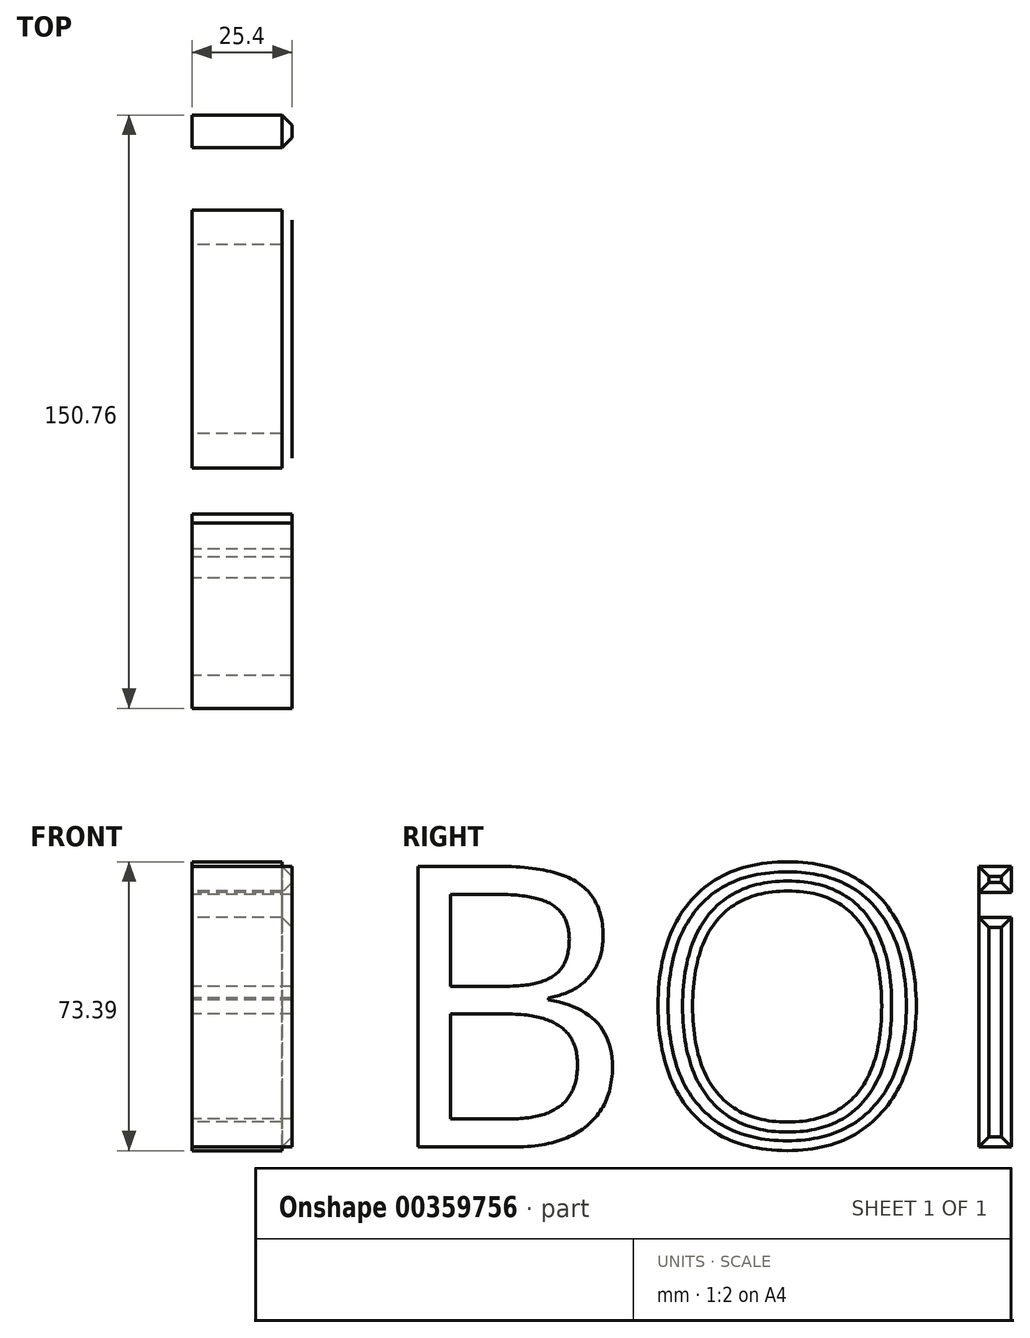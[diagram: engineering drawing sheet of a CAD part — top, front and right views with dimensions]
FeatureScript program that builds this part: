
annotation { "Feature Type Name" : "Feature", "Feature Type Description" : "" }
export const myFeature = defineFeature(function(context is Context, id is Id, definition is map)
    precondition{}
    {
        {
            var Q0;
            Q0=qCreatedBy(makeId("Right.planeOp"),FACE);
            var sketch = newSketch(context, id + "F0", { "sketchPlane" : qUnion([Q0])});
            skText(sketch, "E0", { "text": "BOI\n", "fontName": "OpenSans-Regular.ttf"});
            const initialGuessF0  = {"E0": [-0.0584, -0.03796, 1, 0, 0.0719]};
            skSetInitialGuess(sketch, initialGuessF0);
            skSolve(sketch);
        }
        {
            var Q0;
            Q0 = qSketchRegion(id + "F0", true);
            extrude(context, id + "F1", {"entities" : qUnion([Q0]), "endBound" : BoundingType.SYMMETRIC, "depth" : 25.4 * mm});
        }
        {
            var Q0;
            Q0=makeQuery(id+"F1.opExtrude","CAP_FACE",FACE,{"disambiguationData":[OSD([sQuery(id+"F0.wireOp",EDGE,"E0.sketch_text.stroke-41"),sQuery(id+"F0.wireOp",EDGE,"E0.sketch_text.stroke-42"),sQuery(id+"F0.wireOp",EDGE,"E0.sketch_text.stroke-43"),sQuery(id+"F0.wireOp",EDGE,"E0.sketch_text.stroke-44")])],"isStart":false});
            var sketch = newSketch(context, id + "F2", { "sketchPlane" : qUnion([Q0])});
            skLineSegment(sketch, "E1.bottom", {"start": v(93.88, 26.68) * mm, "end": v(102.17, 26.68) * mm});
            skLineSegment(sketch, "E1.top", {"start": v(93.88, 20.3) * mm, "end": v(102.17, 20.3) * mm});
            skLineSegment(sketch, "E1.left", {"start": v(93.88, 26.68) * mm, "end": v(93.88, 20.3) * mm});
            skLineSegment(sketch, "E1.right", {"start": v(102.17, 26.68) * mm, "end": v(102.17, 20.3) * mm});
            skSolve(sketch);
        }
        {
            var Q0;
            Q0=makeQuery(id+"F2.imprint","IMPRINT",FACE,{"disambiguationData":[TD([[makeQuery(id+"F2.imprint","IMPRINT",EDGE,{"derivedFrom":sQuery(id+"F2.wireOp",EDGE,"E1.bottom")}),-1.0]])]});
            extrude(context, id + "F3", {"entities" : qUnion([Q0]), "operationType" : NewBodyOperationType.REMOVE, "oppositeDirection" : true, "depth" : 25.4 * mm});
        }
        {
            var Q0;
            Q0=makeQuery(id+"F1.opExtrude","CAP_FACE",FACE,{"disambiguationData":[OSD([sQuery(id+"F0.wireOp",EDGE,"E0.sketch_text.stroke-0"),sQuery(id+"F0.wireOp",EDGE,"E0.sketch_text.stroke-1"),sQuery(id+"F0.wireOp",EDGE,"E0.sketch_text.stroke-2"),sQuery(id+"F0.wireOp",EDGE,"E0.sketch_text.stroke-3"),sQuery(id+"F0.wireOp",EDGE,"E0.sketch_text.stroke-4"),sQuery(id+"F0.wireOp",EDGE,"E0.sketch_text.stroke-5"),sQuery(id+"F0.wireOp",EDGE,"E0.sketch_text.stroke-6"),sQuery(id+"F0.wireOp",EDGE,"E0.sketch_text.stroke-7"),sQuery(id+"F0.wireOp",EDGE,"E0.sketch_text.stroke-8"),sQuery(id+"F0.wireOp",EDGE,"E0.sketch_text.stroke-9"),sQuery(id+"F0.wireOp",EDGE,"E0.sketch_text.stroke-10"),sQuery(id+"F0.wireOp",EDGE,"E0.sketch_text.stroke-11"),sQuery(id+"F0.wireOp",EDGE,"E0.sketch_text.stroke-12"),sQuery(id+"F0.wireOp",EDGE,"E0.sketch_text.stroke-13"),sQuery(id+"F0.wireOp",EDGE,"E0.sketch_text.stroke-14"),sQuery(id+"F0.wireOp",EDGE,"E0.sketch_text.stroke-15"),sQuery(id+"F0.wireOp",EDGE,"E0.sketch_text.stroke-16"),sQuery(id+"F0.wireOp",EDGE,"E0.sketch_text.stroke-17"),sQuery(id+"F0.wireOp",EDGE,"E0.sketch_text.stroke-18"),sQuery(id+"F0.wireOp",EDGE,"E0.sketch_text.stroke-19"),sQuery(id+"F0.wireOp",EDGE,"E0.sketch_text.stroke-20"),sQuery(id+"F0.wireOp",EDGE,"E0.sketch_text.stroke-21"),sQuery(id+"F0.wireOp",EDGE,"E0.sketch_text.stroke-22"),sQuery(id+"F0.wireOp",EDGE,"E0.sketch_text.stroke-23"),sQuery(id+"F0.wireOp",EDGE,"E0.sketch_text.stroke-24")])],"isStart":false});
            var Q1;
            Q1=makeQuery(id+"F1.opExtrude","CAP_FACE",FACE,{"disambiguationData":[OSD([sQuery(id+"F0.wireOp",EDGE,"E0.sketch_text.stroke-25"),sQuery(id+"F0.wireOp",EDGE,"E0.sketch_text.stroke-26"),sQuery(id+"F0.wireOp",EDGE,"E0.sketch_text.stroke-27"),sQuery(id+"F0.wireOp",EDGE,"E0.sketch_text.stroke-28"),sQuery(id+"F0.wireOp",EDGE,"E0.sketch_text.stroke-29"),sQuery(id+"F0.wireOp",EDGE,"E0.sketch_text.stroke-30"),sQuery(id+"F0.wireOp",EDGE,"E0.sketch_text.stroke-31"),sQuery(id+"F0.wireOp",EDGE,"E0.sketch_text.stroke-32"),sQuery(id+"F0.wireOp",EDGE,"E0.sketch_text.stroke-33"),sQuery(id+"F0.wireOp",EDGE,"E0.sketch_text.stroke-34"),sQuery(id+"F0.wireOp",EDGE,"E0.sketch_text.stroke-35"),sQuery(id+"F0.wireOp",EDGE,"E0.sketch_text.stroke-36"),sQuery(id+"F0.wireOp",EDGE,"E0.sketch_text.stroke-37"),sQuery(id+"F0.wireOp",EDGE,"E0.sketch_text.stroke-38"),sQuery(id+"F0.wireOp",EDGE,"E0.sketch_text.stroke-39"),sQuery(id+"F0.wireOp",EDGE,"E0.sketch_text.stroke-40")])],"isStart":false});
            var Q2;
            {var subQ0=sQuery(id+"F0.wireOp",EDGE,"E0.sketch_text.stroke-41");var subQ1=sQuery(id+"F0.wireOp",EDGE,"E0.sketch_text.stroke-44");var subQ2=sQuery(id+"F0.wireOp",EDGE,"E0.sketch_text.stroke-43");Q2=makeQuery(id+"F3.boolean.opBoolean","SPLIT",FACE,{"disambiguationData":[TD([makeQuery(id+"F1.opExtrude","SWEPT_FACE",FACE,{"disambiguationData":[OSD([subQ1])]})])],"derivedFrom":makeQuery(id+"F1.opExtrude","CAP_FACE",FACE,{"disambiguationData":[OSD([subQ0,sQuery(id+"F0.wireOp",EDGE,"E0.sketch_text.stroke-42"),subQ2,subQ1])],"isStart":false})});}
            var Q3;
            {var subQ0=sQuery(id+"F0.wireOp",EDGE,"E0.sketch_text.stroke-41");var subQ1=sQuery(id+"F0.wireOp",EDGE,"E0.sketch_text.stroke-42");var subQ2=sQuery(id+"F0.wireOp",EDGE,"E0.sketch_text.stroke-43");Q3=makeQuery(id+"F3.boolean.opBoolean","SPLIT",FACE,{"disambiguationData":[TD([makeQuery(id+"F1.opExtrude","SWEPT_FACE",FACE,{"disambiguationData":[OSD([subQ1])]})])],"derivedFrom":makeQuery(id+"F1.opExtrude","CAP_FACE",FACE,{"disambiguationData":[OSD([subQ0,subQ1,subQ2,sQuery(id+"F0.wireOp",EDGE,"E0.sketch_text.stroke-44")])],"isStart":false})});}
            chamfer(context, id + "F4", {"entities" : qUnion([Q0, Q1, Q2, Q3]), "width" : 2.54 * mm, "tangentPropagation" : true});
        }
    });
